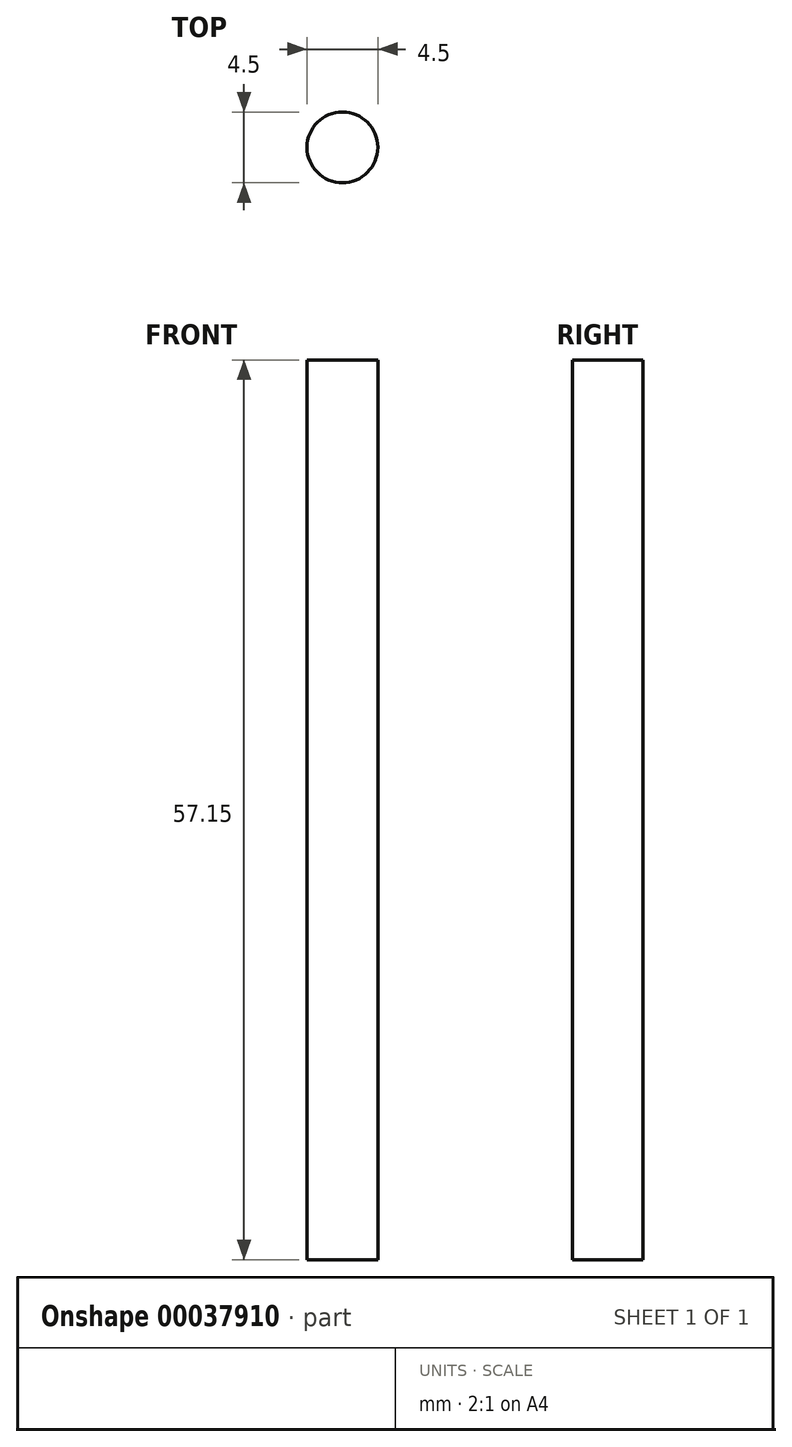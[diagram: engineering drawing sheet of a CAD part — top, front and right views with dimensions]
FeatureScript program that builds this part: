
annotation { "Feature Type Name" : "Feature", "Feature Type Description" : "" }
export const myFeature = defineFeature(function(context is Context, id is Id, definition is map)
    precondition{}
    {
        {
            var Q0;
            Q0=qCreatedBy(makeId("Top.planeOp"),FACE);
            var sketch = newSketch(context, id + "F0", { "sketchPlane" : qUnion([Q0])});
            skCircle(sketch, "E0", {"center": v(0, 0) * mm, "radius": 2.25 * mm});
            skSolve(sketch);
        }
        {
            var Q0;
            Q0 = qSketchRegion(id + "F0", true);
            extrude(context, id + "F1", {"entities" : qUnion([Q0]), "depth" : 57.15 * mm});
        }
    });
